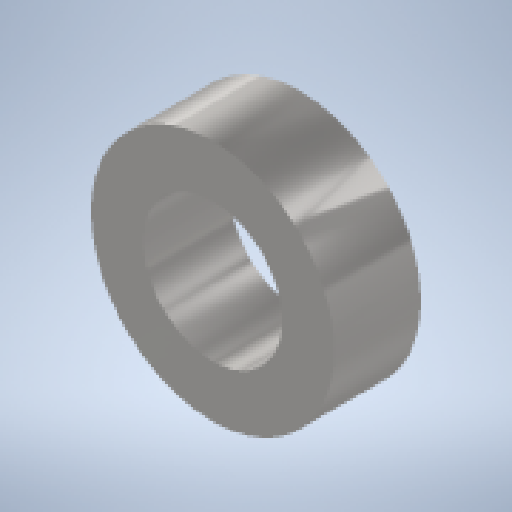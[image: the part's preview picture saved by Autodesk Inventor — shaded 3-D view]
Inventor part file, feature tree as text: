
AUTODESK INVENTOR PART (.ipt)
format: ipt  version: 2024 (Build 280153000, 153)  size: 141,312 bytes
history: native  units: mm
features: other x1, extrude x1, sketch x1
ambient origin geometry x8: Origin, YZ Plane, XZ Plane, XY Plane, X Axis, Y Axis, Z Axis, Center Point
bodies: Body1 (feature_tree)
feature tree (3):
  other  "ソリッド1"
  extrude  "押し出し1"  Depth=4.0mm
  sketch  "スケッチ1"
